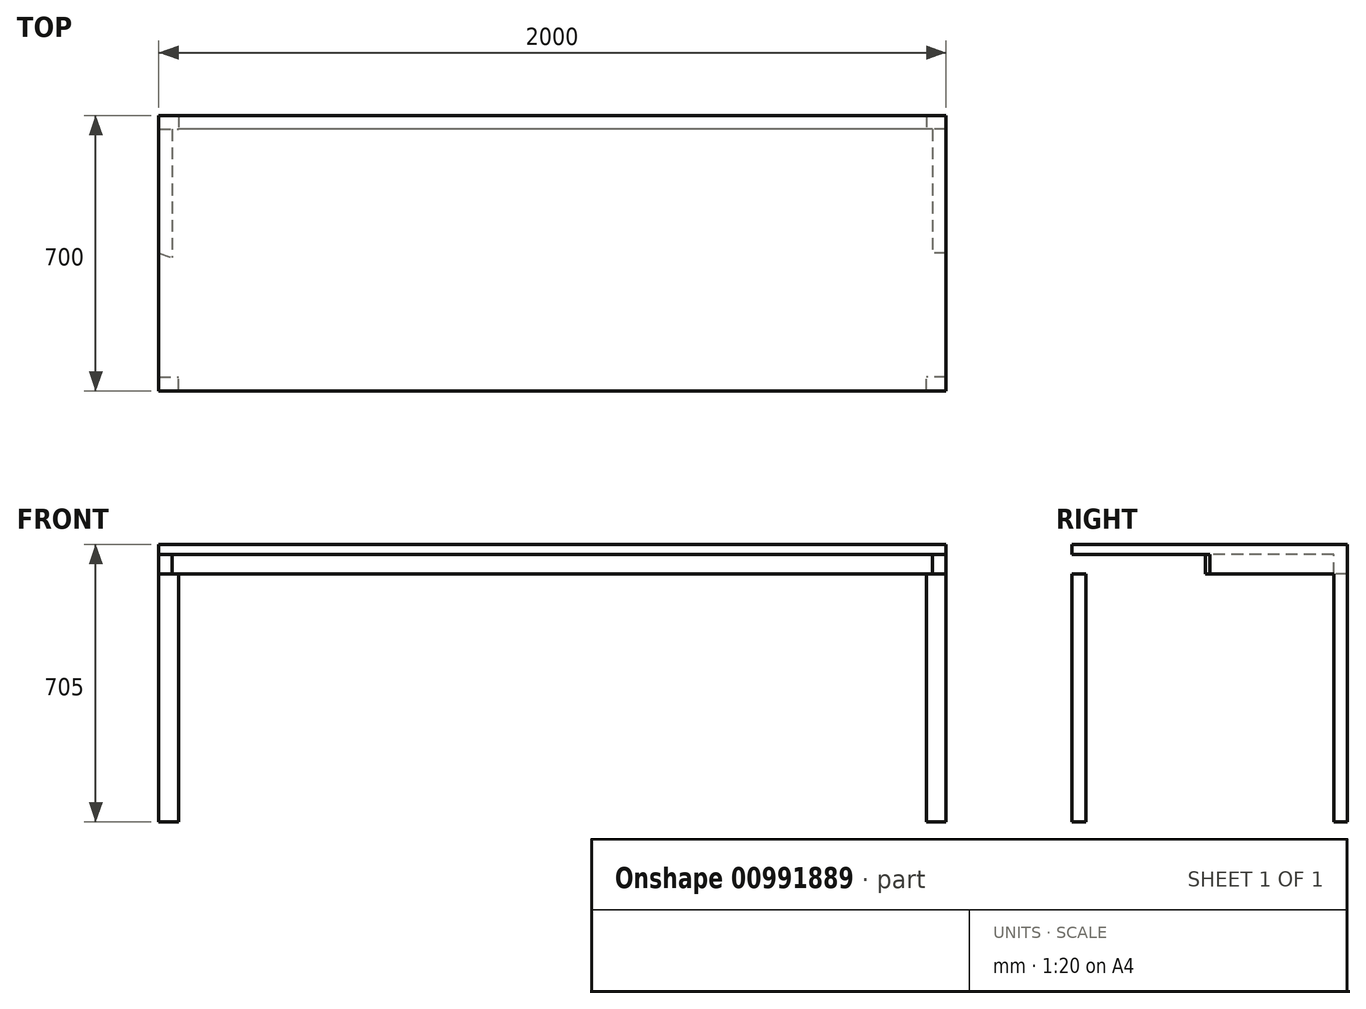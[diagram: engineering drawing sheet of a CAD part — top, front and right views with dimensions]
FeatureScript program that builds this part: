
annotation { "Feature Type Name" : "Feature", "Feature Type Description" : "" }
export const myFeature = defineFeature(function(context is Context, id is Id, definition is map)
    precondition{}
    {
        {
            var Q0;
            Q0=qCreatedBy(makeId("Top.planeOp"),FACE);
            var sketch = newSketch(context, id + "F0", { "sketchPlane" : qUnion([Q0])});
            skLineSegment(sketch, "E0.bottom", {"start": v(-613.13, 360.94) * mm, "end": v(1386.87, 360.94) * mm});
            skLineSegment(sketch, "E0.top", {"start": v(-613.13, -339.06) * mm, "end": v(1386.87, -339.06) * mm});
            skLineSegment(sketch, "E0.left", {"start": v(-613.13, 360.94) * mm, "end": v(-613.13, -339.06) * mm});
            skLineSegment(sketch, "E0.right", {"start": v(1386.87, 360.94) * mm, "end": v(1386.87, -339.06) * mm});
            skSolve(sketch);
        }
        {
            var Q0;
            Q0 = qSketchRegion(id + "F0", true);
            extrude(context, id + "F1", {"entities" : qUnion([Q0]), "depth" : 25 * mm, "offsetDistance" : 25 * mm});
        }
        {
            var Q0;
            Q0=makeQuery(id+"F1.opExtrude","CAP_FACE",FACE,{"disambiguationData":[OSD([sQuery(id+"F0.wireOp",EDGE,"E0.bottom"),sQuery(id+"F0.wireOp",EDGE,"E0.top"),sQuery(id+"F0.wireOp",EDGE,"E0.left"),sQuery(id+"F0.wireOp",EDGE,"E0.right")])],"isStart":true});
            var sketch = newSketch(context, id + "F2", { "sketchPlane" : qUnion([Q0])});
            skLineSegment(sketch, "E1", {"start": v(1052.86, -360.94) * mm, "end": v(1052.86, -325.94) * mm});
            skLineSegment(sketch, "E2", {"start": v(1052.86, 339.06) * mm, "end": v(1052.86, 304.06) * mm});
            skLineSegment(sketch, "E3", {"start": v(1052.86, 304.06) * mm, "end": v(1052.86, 339.06) * mm});
            skLineSegment(sketch, "E4", {"start": v(1386.87, -10.94) * mm, "end": v(1351.87, -10.94) * mm});
            skLineSegment(sketch, "E5", {"start": v(-613.13, -10.94) * mm, "end": v(-579.89, 0) * mm});
            skLineSegment(sketch, "E6.bottom", {"start": v(1351.87, -325.94) * mm, "end": v(-579.89, -325.94) * mm});
            skLineSegment(sketch, "E6.top", {"start": v(1351.87, 304.06) * mm, "end": v(-579.89, 304.06) * mm});
            skLineSegment(sketch, "E6.left", {"start": v(1351.87, -325.94) * mm, "end": v(1351.87, 304.06) * mm});
            skLineSegment(sketch, "E6.right", {"start": v(-579.89, -325.94) * mm, "end": v(-579.89, 304.06) * mm});
            skSolve(sketch);
        }
        {
            var Q0;
            {var subQ4=sQuery(id+"F2.wireOp",EDGE,"E1");Q0=makeQuery(id+"F2.imprint","IMPRINT",FACE,{"disambiguationData":[TD([[makeQuery(id+"F2.imprint","IMPRINT",EDGE,{"derivedFrom":subQ4}),1.0]])]});}
            var Q1;
            {var subQ4=sQuery(id+"F2.wireOp",EDGE,"E1");Q1=makeQuery(id+"F2.imprint","IMPRINT",FACE,{"disambiguationData":[TD([[makeQuery(id+"F2.imprint","IMPRINT",EDGE,{"derivedFrom":subQ4}),-1.0]])]});}
            var Q2;
            {var subQ4=sQuery(id+"F2.wireOp",EDGE,"E3");Q2=makeQuery(id+"F2.imprint","IMPRINT",FACE,{"disambiguationData":[TD([[makeQuery(id+"F2.imprint","IMPRINT",EDGE,{"derivedFrom":subQ4}),-1.0]])]});}
            var Q3;
            {var subQ1=sQuery(id+"F2.wireOp",EDGE,"E3");Q3=makeQuery(id+"F2.imprint","IMPRINT",FACE,{"disambiguationData":[TD([[makeQuery(id+"F2.imprint","IMPRINT",EDGE,{"derivedFrom":subQ1}),1.0]])]});}
            extrude(context, id + "F3", {"entities" : qUnion([Q0, Q1, Q2, Q3]), "operationType" : NewBodyOperationType.ADD, "depth" : 50 * mm, "offsetDistance" : 25 * mm});
        }
        {
            var Q0;
            Q0=makeQuery(id+"F1.opExtrude","CAP_FACE",FACE,{"disambiguationData":[OSD([sQuery(id+"F0.wireOp",EDGE,"E0.bottom"),sQuery(id+"F0.wireOp",EDGE,"E0.top"),sQuery(id+"F0.wireOp",EDGE,"E0.left"),sQuery(id+"F0.wireOp",EDGE,"E0.right")])],"isStart":true});
            var sketch = newSketch(context, id + "F4", { "sketchPlane" : qUnion([Q0])});
            skSolve(sketch);
        }
        {
            var Q0;
            Q0=makeQuery(id+"F3.opExtrude","CAP_FACE",FACE,{"disambiguationData":[OSD([sQuery(id+"F0.wireOp",EDGE,"E0.bottom"),sQuery(id+"F0.wireOp",EDGE,"E0.top"),sQuery(id+"F0.wireOp",EDGE,"E0.left"),sQuery(id+"F0.wireOp",EDGE,"E0.right"),sQuery(id+"F2.wireOp",EDGE,"E6.bottom"),sQuery(id+"F2.wireOp",EDGE,"E6.top"),sQuery(id+"F2.wireOp",EDGE,"E6.left"),sQuery(id+"F2.wireOp",EDGE,"E6.right")])],"isStart":false});
            var sketch = newSketch(context, id + "F5", { "sketchPlane" : qUnion([Q0])});
            skLineSegment(sketch, "E7.bottom", {"start": v(-613.13, 339.06) * mm, "end": v(-563.13, 339.06) * mm});
            skLineSegment(sketch, "E7.top", {"start": v(-613.13, 304.06) * mm, "end": v(-563.13, 304.06) * mm});
            skLineSegment(sketch, "E7.left", {"start": v(-613.13, 339.06) * mm, "end": v(-613.13, 304.06) * mm});
            skLineSegment(sketch, "E7.right", {"start": v(-563.13, 339.06) * mm, "end": v(-563.13, 304.06) * mm});
            skLineSegment(sketch, "E8.bottom", {"start": v(-613.13, -360.94) * mm, "end": v(-563.13, -360.94) * mm});
            skLineSegment(sketch, "E8.top", {"start": v(-613.13, -325.94) * mm, "end": v(-563.13, -325.94) * mm});
            skLineSegment(sketch, "E8.left", {"start": v(-613.13, -360.94) * mm, "end": v(-613.13, -325.94) * mm});
            skLineSegment(sketch, "E8.right", {"start": v(-563.13, -360.94) * mm, "end": v(-563.13, -325.94) * mm});
            skLineSegment(sketch, "E9.bottom", {"start": v(1386.87, -360.94) * mm, "end": v(1336.87, -360.94) * mm});
            skLineSegment(sketch, "E9.top", {"start": v(1386.87, -325.94) * mm, "end": v(1336.87, -325.94) * mm});
            skLineSegment(sketch, "E9.left", {"start": v(1386.87, -360.94) * mm, "end": v(1386.87, -325.94) * mm});
            skLineSegment(sketch, "E9.right", {"start": v(1336.87, -360.94) * mm, "end": v(1336.87, -325.94) * mm});
            skLineSegment(sketch, "E10.bottom", {"start": v(1386.87, 339.06) * mm, "end": v(1336.87, 339.06) * mm});
            skLineSegment(sketch, "E10.top", {"start": v(1386.87, 304.06) * mm, "end": v(1336.87, 304.06) * mm});
            skLineSegment(sketch, "E10.left", {"start": v(1386.87, 339.06) * mm, "end": v(1386.87, 304.06) * mm});
            skLineSegment(sketch, "E10.right", {"start": v(1336.87, 339.06) * mm, "end": v(1336.87, 304.06) * mm});
            skSolve(sketch);
        }
        {
            var Q0;
            Q0 = qSketchRegion(id + "F5", true);
            extrude(context, id + "F6", {"entities" : qUnion([Q0]), "operationType" : NewBodyOperationType.ADD, "depth" : 630 * mm, "offsetDistance" : 25 * mm});
        }
    });
